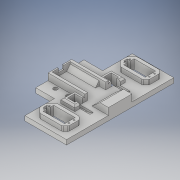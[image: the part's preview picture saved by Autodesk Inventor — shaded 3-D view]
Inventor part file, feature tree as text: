
AUTODESK INVENTOR PART (.ipt)
format: ipt  version: 2018 (Build 220112000, 112)  size: 579,072 bytes
history: native  units: in
note: dims shown in document units (in); Inventor stores cm internally (conversion verified against a paired STEP export)
features: extrude x28, sketch x28, chamfer x4, fillet x2
ambient origin geometry x8: Origin, YZ Plane, XZ Plane, XY Plane, X Axis, Y Axis, Z Axis, Center Point
bodies: Solid1 (feature_tree)
feature tree (62):
  extrude  "Extrusion1"  Depth=4.5in
  extrude  "Extrusion2"  Depth=1.75in
  chamfer  "Chamfer1"  Distance=0.4in
  extrude  "Extrusion3"  Depth=0.25in
  extrude  "Extrusion4"  Depth=0.25in
  fillet  "Fillet1"  Radius=0.25in
  extrude  "Extrusion5"  Depth=0.25in
  extrude  "Extrusion6"  Depth=0.125in TaperAngle=45.0deg
  extrude  "Extrusion7"  Depth=0.125in
  extrude  "Extrusion8"  Depth=0.25in
  extrude  "Extrusion9"  Depth=1.0in
  extrude  "Extrusion10"  Depth=0.25in
  extrude  "Extrusion11"  Depth=0.15in TaperAngle=0.0deg
  extrude  "Extrusion12"  Depth=1.75in
  extrude  "Extrusion13"  Depth=3.95in
  extrude  "Extrusion14"  Depth=1.35in
  extrude  "Extrusion15"  Depth=0.2in
  extrude  "Extrusion16"  Depth=0.35in
  extrude  "Extrusion17"  Depth=3.95in TaperAngle=0.0deg
  extrude  "Extrusion18"  Depth=0.5in TaperAngle=0.0deg
  extrude  "Extrusion25"  Depth=0.25in TaperAngle=0.0deg
  extrude  "Extrusion26"  Depth=0.2in TaperAngle=0.0deg
  chamfer  "Chamfer4"  Distance=0.5in
  extrude  "Extrusion27"  Depth=0.25in
  extrude  "Extrusion28"  Depth=0.35in
  extrude  "Extrusion29"  Depth=2.5in TaperAngle=0.0deg
  extrude  "Extrusion31"  Depth=0.3in
  extrude  "Extrusion32"  Depth=0.3in
  extrude  "Extrusion35"  Depth=0.3in
  extrude  "Extrusion36"  Depth=0.3in
  extrude  "Extrusion37"  Depth=0.8in
  chamfer  "Chamfer6"  Distance=1.75in
  chamfer  "Chamfer7"  Distance=0.25in
  fillet  "Fillet2"  Radius=0.8in
  sketch  "Sketch1"  dims[d0=6.0in d1=4.5in]
  sketch  "Sketch2"  dims[d2=1.75in d3=1.75in]
  sketch  "Sketch3"  dims[d4=0.55in]
  sketch  "Sketch4"  dims[d5=0.55in]
  sketch  "Sketch5"  dims[d6=0.55in]
  sketch  "Sketch6"  dims[d7=0.55in]
  sketch  "Sketch7"  dims[d8=2.15in]
  sketch  "Sketch8"  dims[d9=1.375in d10=0.4in d11=0.0in]
  sketch  "Sketch9"  dims[d12=0.25in d13=0.25in]
  sketch  "Sketch10"  dims[d14=0.25in d15=0.25in d16=0.25in]
  sketch  "Sketch11"  dims[d17=0.25in d18=0.25in]
  sketch  "Sketch12"  dims[d19=0.35in d20=0.0in d21=0.125in d22=0.125in d23=45.0deg]
  sketch  "Sketch13"  dims[d24=0.25in d25=0.125in]
  sketch  "Sketch14"  dims[d26=0.125in d27=0.25in]
  sketch  "Sketch15"  dims[d28=0.35in d29=0.0in d30=1.0in]
  sketch  "Sketch16"  dims[d31=0.25in d32=0.25in]
  sketch  "Sketch17"  dims[d33=1.0in d34=0.15in d35=0.0in]
  sketch  "Sketch18"  dims[d36=0.84in d37=1.75in]
  sketch  "Sketch25"  dims[d38=0.05in d39=3.95in]
  sketch  "Sketch26"  dims[d40=0.5in d41=0.0in d42=1.35in]
  sketch  "Sketch27"  dims[d43=0.2in d44=0.82in]
  sketch  "Sketch28"  dims[d45=0.35in d46=0.35in]
  sketch  "Sketch29"  dims[d47=0.265in d48=3.95in d49=0.0in]
  sketch  "Sketch30"  dims[d50=0.15in d51=0.5in d52=0.0in]
  sketch  "Sketch31"  dims[d53=0.5in d54=0.0in d55=0.25in d56=0.0in]
  sketch  "Sketch32"  dims[d57=0.3in d58=0.0in d59=0.2in d60=0.0in]
  sketch  "Sketch33"  dims[d61=2.25in d62=0.5in d63=0.0in]
  sketch  "Sketch34"  dims[d64=1.25in d65=0.0in d66=0.25in d67=0.35in d68=2.5in d69=0.0in d70=0.3in d71=0.3in d72=0.3in d73=0.3in d74=0.8in d75=1.75in d76=0.25in d77=0.8in d78=1.75in d79=0.25in d80=0.25in d81=0.25in d82=0.4in d83=0.0in d84=1.0in d85=0.0in d86=1.0in d87=0.0in d88=0.0in d89=4.5in d90=0.05in d91=0.0in d138=0.121in d139=0.0in d140=0.0in d141=0.6in d142=0.51in d143=0.0in d144=0.6in d145=0.51in d146=45.0deg d147=0.01in d148=0.0in d149=0.1in d150=0.5in d151=0.0in d152=0.23in d153=0.21in d154=0.21in d155=0.0in d156=0.5in d157=0.0in d158=0.781in d159=0.781in d160=1.6in d161=1.6in d162=0.6095in d163=0.75in d164=0.75in d165=0.6095in d168=2.2in d169=2.2in d170=1.4in d171=1.0in d172=0.0in d173=0.3in d174=0.24in d175=0.24in d176=0.3in d177=0.24in d178=0.24in d179=0.3in d180=0.35in d181=0.0in d185=0.18in d186=0.18in d187=0.18in d188=0.18in d189=0.39in d190=0.39in d191=0.4355in d192=0.4355in d193=0.1in d194=0.1in d195=0.1in d196=0.1in d199=0.18in d200=0.18in d201=0.18in d202=0.18in d203=0.1in d204=0.1in d205=0.1in d206=0.1in d207=0.39in d208=0.39in d209=0.4355in d210=0.4355in d213=0.25in d214=0.0in d215=0.05in d217=0.25in d218=0.05in d219=0.25in d220=0.5055in d221=0.5055in d222=1.0in d223=0.0in d224=0.1in d225=0.0in d226=0.25in d227=0.125in d228=45.0deg d229=0.4in d230=0.125in d231=45.0deg d232=0.125in]
